# Revit family: ElectricalFixture_WiringAccessories_Hager_Sollyster_WMPS12W
name_source: partatom
category: Lighting Fixtures
revit_build: Autodesk Revit 2015 (Build: 20160512_1515(x64)
units: mm (PartAtom-declared; Revit-internal decimal feet)

## types (1)
- WMPS12W
    CE Approval = Yes
    Colour = SollystaWhite
    Default Elevation = 1219.2 mm  [stored 4 ft]
    Description = 10AX 1 Gang 2 Way Wall Switch Wide Rocker
    Design Country = China
    EAN Code = 5015652261735
    Expected Life = 25 years
    Extrusion From Wall = 11.9 mm
    Features = 10AX 1 Gang 2 Way Wall Switch Wide Rocker
    Finish = Gloss
    Frequency = 50/60Hz
    Gross Weight kg = 0.165
    LED Indicator Switch = No
    Manufacturer = Hager
    Manufacturer Country = United Kingdom
    Manufacturer Website = http://www.hager.co.uk
    Material = Urea Formaldehyde Thermoset Plastic
    Name = WhiteMoldedSocket_10AXWallSwitches_WMPS12W
    Overall Depth = 26.1 mm
    Overall Height = 86 mm  [stored 0.282152 ft]
    Overall Length = 86 mm  [stored 0.282152 ft]
    Overall Width = 86 mm  [stored 0.282152 ft]
    Packaging Recyclable = Yes
    Product Family = WhiteMouldedSockets_10AXWallSwitches
    Product Group = WiringAccessories
    Product Literature = http://www.hager.co.uk
    Product Model Number = WMPS12W
    Product Range = Sollysta
    Product URL = http://www.hager.co.uk
    Reference Standard = BS 1363-2
    Shape = Rectangular
    Shipping Weight kg = 0.188
    Supply Phase = 1
    Switch = Yes
    Technical Description = 10AX 1 Gang 2 Way Wall Switch Wide Rocker
    Type = ElectricalFixture
    Unique Reference = WMPS12W
    Voltage (Volts) = 230V/240V

note: [stored X ft] marks values corroborated as IEEE doubles in the binary element streams (Revit-internal decimal feet)

## geometry (parser evidence)
native form markers: Blend x4, Sweep x9
no freeform markers — native parametric forms only
